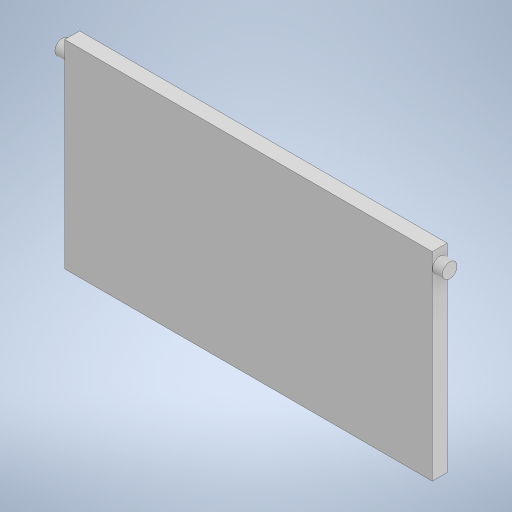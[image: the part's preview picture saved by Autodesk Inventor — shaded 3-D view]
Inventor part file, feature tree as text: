
AUTODESK INVENTOR PART (.ipt)
format: ipt  version: 2023.1 (Build 271208000, 208)  size: 205,312 bytes
history: native  units: mm
features: extrude x2, sketch x2, mirror x1
ambient origin geometry x8: Origin, YZ Plane, XZ Plane, XY Plane, X Axis, Y Axis, Z Axis, Center Point
bodies: 实体1 (feature_tree)
feature tree (5):
  extrude  "拉伸1"  Depth=200.0mm
  extrude  "拉伸2"  Depth=15.0mm
  mirror  "镜像1"
  sketch  "草图1"  dims[d0=15.0mm d1=200.0mm]
  sketch  "草图2"  dims[d2=370.0mm d3=0.0mm d4=15.0mm d5=15.0mm d6=10.0mm d7=0.0mm]
